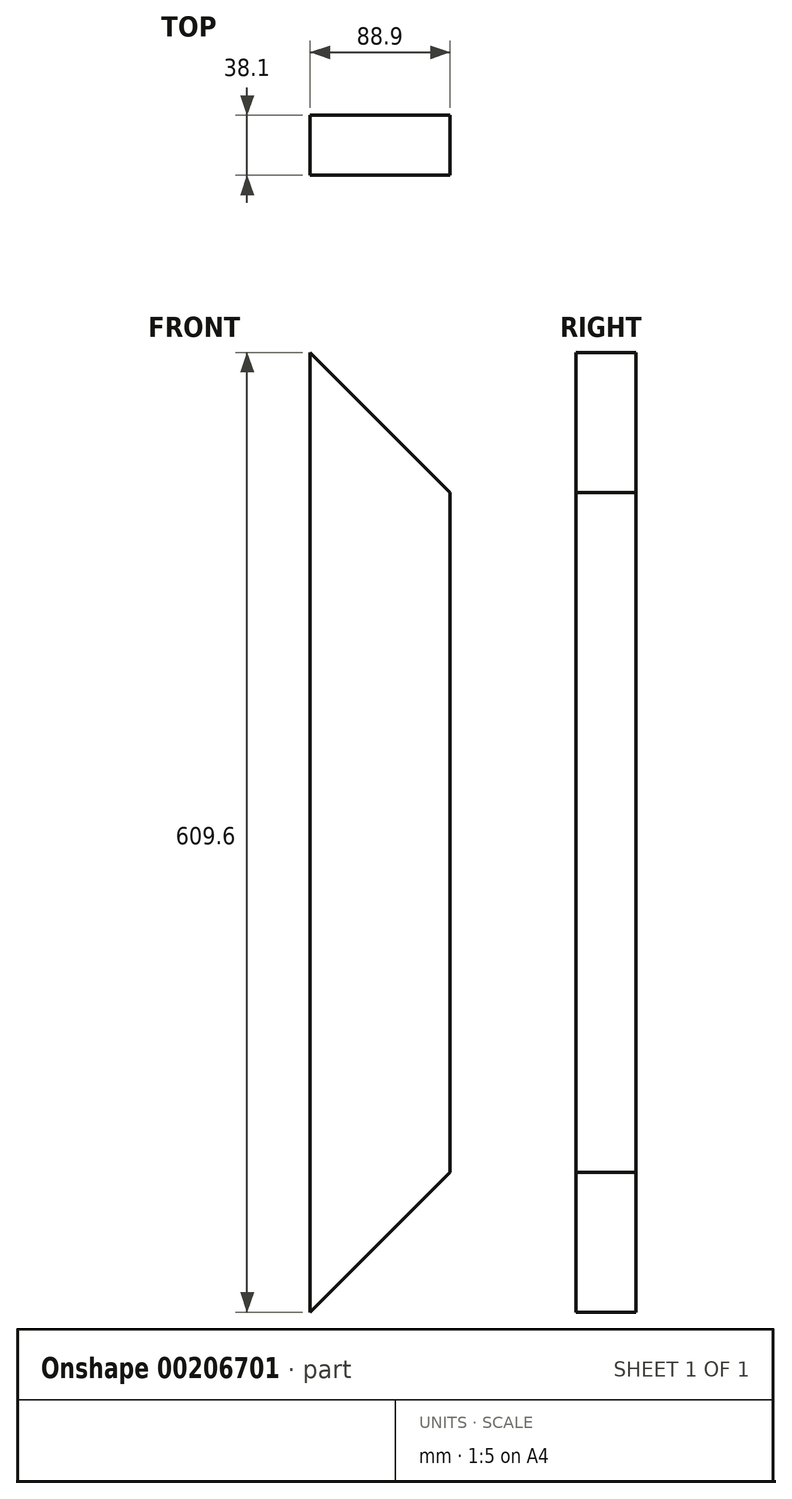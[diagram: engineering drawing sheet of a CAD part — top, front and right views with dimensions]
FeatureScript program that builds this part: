
annotation { "Feature Type Name" : "Feature", "Feature Type Description" : "" }
export const myFeature = defineFeature(function(context is Context, id is Id, definition is map)
    precondition{}
    {
        {
            var Q0;
            Q0=qCreatedBy(makeId("Top.planeOp"),FACE);
            var sketch = newSketch(context, id + "F0", { "sketchPlane" : qUnion([Q0])});
            skLineSegment(sketch, "E0.bottom", {"start": v(44.45, 19.05) * mm, "end": v(-44.45, 19.05) * mm});
            skLineSegment(sketch, "E0.top", {"start": v(44.45, -19.05) * mm, "end": v(-44.45, -19.05) * mm});
            skLineSegment(sketch, "E0.left", {"start": v(44.45, 19.05) * mm, "end": v(44.45, -19.05) * mm});
            skLineSegment(sketch, "E0.right", {"start": v(-44.45, 19.05) * mm, "end": v(-44.45, -19.05) * mm});
            skPoint(sketch, "E0.middle", {"position": v(0, 0) * mm});
            skSolve(sketch);
        }
        {
            var Q0;
            Q0 = qSketchRegion(id + "F0", true);
            extrude(context, id + "F1", {"entities" : qUnion([Q0]), "endBound" : BoundingType.SYMMETRIC, "depth" : 609.6 * mm});
        }
        {
            var Q0;
            Q0=makeQuery(id+"F1.opExtrude","SWEPT_FACE",FACE,{"disambiguationData":[OSD([sQuery(id+"F0.wireOp",EDGE,"E0.bottom")])]});
            var sketch = newSketch(context, id + "F2", { "sketchPlane" : qUnion([Q0])});
            skLineSegment(sketch, "E1", {"start": v(44.45, 304.8) * mm, "end": v(-44.45, 304.8) * mm});
            skLineSegment(sketch, "E2", {"start": v(-44.45, 304.8) * mm, "end": v(-44.45, 215.9) * mm});
            skLineSegment(sketch, "E3", {"start": v(-44.45, 215.9) * mm, "end": v(44.45, 304.8) * mm});
            skLineSegment(sketch, "E4", {"start": v(44.45, -304.8) * mm, "end": v(-44.45, -304.8) * mm});
            skLineSegment(sketch, "E5", {"start": v(-44.45, -304.8) * mm, "end": v(-44.45, -215.9) * mm});
            skLineSegment(sketch, "E6", {"start": v(-44.45, -215.9) * mm, "end": v(44.45, -304.8) * mm});
            skSolve(sketch);
        }
        {
            var Q0;
            Q0 = qSketchRegion(id + "F2", true);
            extrude(context, id + "F3", {"entities" : qUnion([Q0]), "operationType" : NewBodyOperationType.REMOVE, "endBound" : BoundingType.THROUGH_ALL, "oppositeDirection" : true, "depth" : 25.4 * mm});
        }
    });
